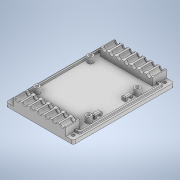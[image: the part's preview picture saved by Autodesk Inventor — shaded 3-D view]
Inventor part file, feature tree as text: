
AUTODESK INVENTOR PART (.ipt)
format: ipt  version: 2021 (Build 250183000, 183)  size: 579,584 bytes
history: native  units: mm
features: extrude x17, sketch x17, fillet x6
ambient origin geometry x8: Origin, YZ Plane, XZ Plane, XY Plane, X Axis, Y Axis, Z Axis, Center Point
bodies: Solid1 (feature_tree)
feature tree (40):
  extrude  "Extrusion1"  Depth=62.0mm
  extrude  "Extrusion2"  Depth=3.0mm
  extrude  "Extrusion3"  Depth=3.0mm
  extrude  "Extrusion4"  Depth=3.0mm
  fillet  "Fillet1"  Radius=6.0mm
  fillet  "Fillet2"  Radius=3.0mm
  fillet  "Fillet3"  Radius=57.4mm
  extrude  "Extrusion7"  Depth=0.8mm
  extrude  "Extrusion8"  Depth=4.8mm
  extrude  "Extrusion9"  Depth=6.0mm
  extrude  "Extrusion10"  Depth=20.0mm
  extrude  "Extrusion11"  Depth=1.0mm
  extrude  "Extrusion12"  Depth=2.0mm TaperAngle=0.0deg
  extrude  "Extrusion13"  TaperAngle=0.0deg  [1 undecoded]
  fillet  "Fillet8"  [1 undecoded]
  fillet  "Fillet9"  Radius=6.0mm
  extrude  "Extrusion14"  TaperAngle=0.0deg  [1 undecoded]
  extrude  "Extrusion15"  Depth=2.0mm
  extrude  "Extrusion16"  Depth=4.0mm
  extrude  "Extrusion17"  Depth=4.0mm
  fillet  "Fillet11"  Radius=2.0mm
  extrude  "Extrusion18"  Depth=2.0mm
  extrude  "Extrusion19"  Depth=35.0mm
  sketch  "Sketch2"  dims[d14=66.0mm d15=62.0mm]
  sketch  "Sketch4"  dims[d16=3.0mm d17=3.0mm]
  sketch  "Sketch5"  dims[d18=3.0mm d19=3.0mm]
  sketch  "Sketch6"  dims[d20=3.0mm d21=4.5mm d22=6.0mm d23=3.0mm d24=57.4mm]
  sketch  "Sketch10"  dims[d25=54.35mm d26=0.8mm]
  sketch  "Sketch11"  dims[d27=51.56mm d28=4.8mm]
  sketch  "Sketch12"  dims[d29=6.0mm d30=6.0mm]
  sketch  "Sketch13"  dims[d31=6.0mm d32=20.0mm]
  sketch  "Sketch14"  dims[d33=20.0mm d34=1.0mm]
  sketch  "Sketch16"  dims[d35=1.0mm d36=2.0mm d37=0.0mm]
  sketch  "Sketch17"  dims[d38=66.0mm d39=62.0mm d40=3.0mm d41=3.0mm d42=3.0mm d43=3.0mm d44=3.0mm d45=4.5mm d46=6.0mm d47=3.0mm d48=57.4mm d49=54.35mm d50=0.8mm d51=51.56mm d52=4.8mm d53=6.0mm d54=6.0mm d55=6.0mm d56=20.0mm d57=20.0mm d58=1.0mm d59=1.0mm d60=0.0mm d61=0.0mm d62=6.0mm d63=0.0mm]
  sketch  "Sketch19"  dims[d64=2.0mm d65=0.0mm]
  sketch  "Sketch20"  dims[d66=2.0mm d67=2.0mm]
  sketch  "Sketch21"  dims[d68=30.0mm d69=4.0mm]
  sketch  "Sketch22"  dims[d70=4.0mm d71=4.0mm d72=2.0mm]
  sketch  "Sketch23"  dims[d73=2.0mm d74=2.0mm]
  sketch  "Sketch24"  dims[d75=2.0mm d76=35.0mm d77=8.0mm d78=0.0mm d79=4.0mm d80=0.0mm d81=1.0mm d82=1.0mm d83=1.0mm d122=15.0mm d123=15.0mm d124=56.0mm d125=4.0mm d126=12.0mm d127=56.0mm d128=4.0mm d129=12.0mm d130=8.0mm d131=0.0mm d132=6.0mm d133=4.0mm d134=70.0mm d136=8.0mm d137=10.0mm d139=10.0mm d141=11.0mm d142=0.0mm d143=6.2mm d144=4.0mm d145=70.0mm d147=8.0mm d148=10.0mm d150=10.0mm d152=11.0mm d153=0.0mm d158=1.0mm d159=1.0mm d160=8.0mm d161=2.0mm d162=0.0mm d163=0.0mm d164=0.0mm d165=4.0mm d166=4.0mm d167=0.0mm d168=2.0mm d169=0.0mm d177=2.0mm d178=2.0mm d179=8.0mm d180=0.0mm d181=2.0mm d182=2.0mm d184=2.0mm d186=2.0mm d187=8.0mm d190=8.0mm d193=8.0mm d196=8.0mm d199=2.0mm d200=2.0mm d201=2.0mm d202=2.0mm d203=2.0mm d204=0.0mm d205=0.5mm d206=0.5mm d211=10.0mm d212=0.0mm d213=2.0mm d214=0.0mm d215=8.0mm d216=5.0mm d217=5.0mm d218=3.0mm d219=8.0mm d220=8.0mm d221=8.0mm d222=5.0mm d223=5.0mm d224=5.0mm d225=5.0mm d226=3.0mm d227=3.0mm d228=3.0mm d229=10.0mm d230=0.0mm d231=7.0mm d232=7.0mm d233=7.0mm d234=7.0mm d235=2.0mm d236=0.0mm d237=2.0mm d238=4.5mm d239=4.0mm d240=70.0mm d242=8.0mm d243=10.0mm d245=10.0mm d247=20.0mm d248=0.0mm d249=4.0mm d250=4.5mm d251=70.0mm d253=8.0mm d254=10.0mm d256=10.0mm d258=20.0mm d259=0.0mm d260=5.0mm d261=5.0mm]
note: 3 required parameter values undecoded (feature->parameter linkage not recoverable at this tier; creation-order binding heuristic only, values carry confidence <= 0.55)
